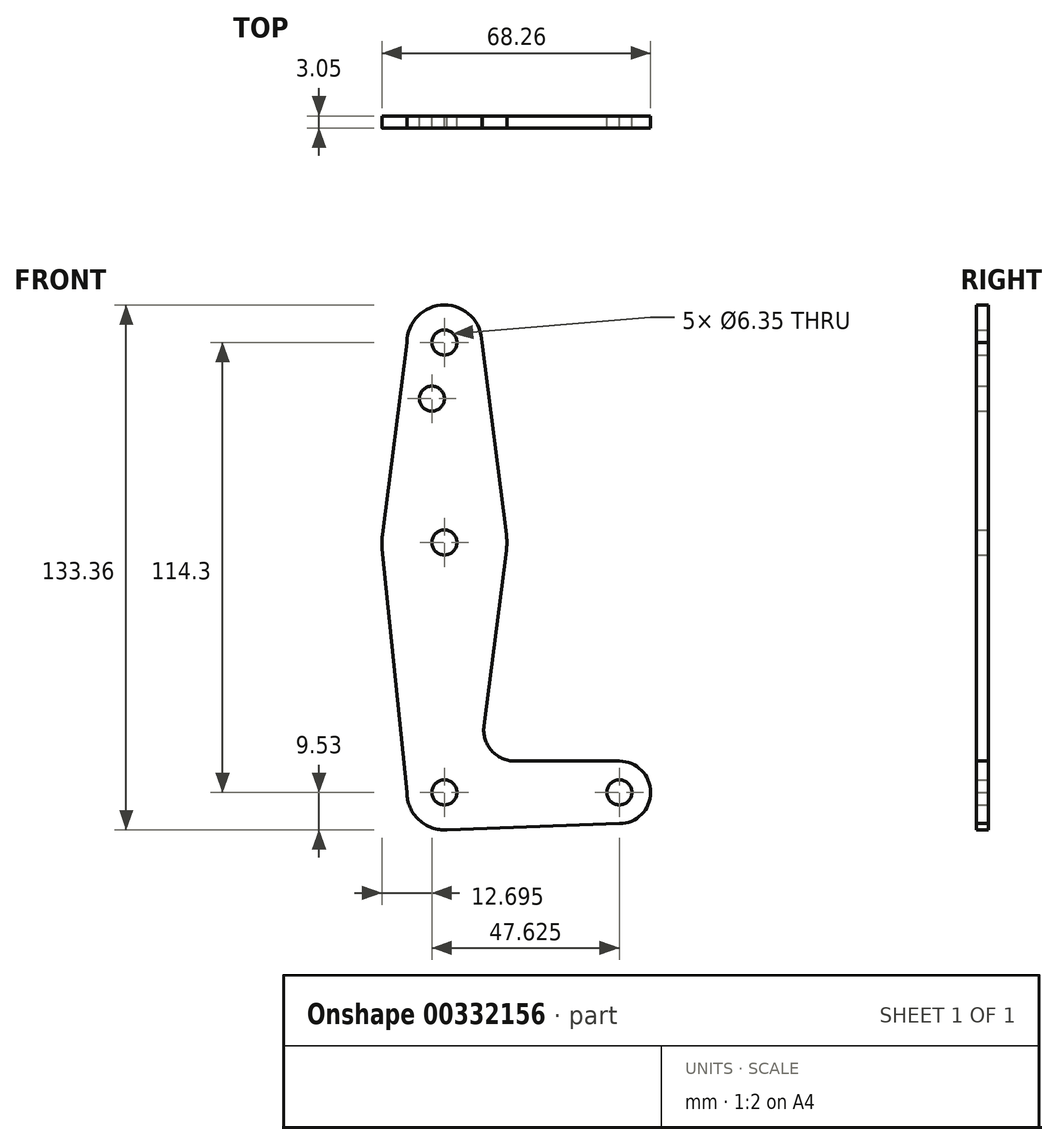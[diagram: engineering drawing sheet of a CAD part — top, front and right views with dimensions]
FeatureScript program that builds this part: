
annotation { "Feature Type Name" : "Feature", "Feature Type Description" : "" }
export const myFeature = defineFeature(function(context is Context, id is Id, definition is map)
    precondition{}
    {
        {
            var Q0;
            Q0=qCreatedBy(makeId("Front.planeOp"),FACE);
            var sketch = newSketch(context, id + "F0", { "sketchPlane" : qUnion([Q0])});
            skCircle(sketch, "E0", {"center": v(0, 0) * mm, "radius": 9.53 * mm});
            skLineSegment(sketch, "E1", {"start": v(0, 0) * mm, "end": v(0, 114.3) * mm, "construction": true});
            skLineSegment(sketch, "E2", {"start": v(0, 0) * mm, "end": v(44.45, 0) * mm, "construction": true});
            skCircle(sketch, "E3", {"center": v(0, 114.3) * mm, "radius": 9.53 * mm});
            skCircle(sketch, "E4", {"center": v(0, 63.5) * mm, "radius": 15.88 * mm});
            skCircle(sketch, "E5", {"center": v(44.45, 0) * mm, "radius": 7.94 * mm});
            skLineSegment(sketch, "E6", {"start": v(-9.53, 114.3) * mm, "end": v(-15.75, 65.5) * mm});
            skLineSegment(sketch, "E7", {"start": v(9.53, 114.3) * mm, "end": v(15.75, 65.5) * mm});
            skLineSegment(sketch, "E8", {"start": v(17.95, 7.94) * mm, "end": v(44.45, 7.94) * mm});
            skLineSegment(sketch, "E9", {"start": v(0, -9.52) * mm, "end": v(44.45, -7.94) * mm});
            skLineSegment(sketch, "E10", {"start": v(10.06, 16.9) * mm, "end": v(15.75, 61.5) * mm});
            skLineSegment(sketch, "E11", {"start": v(-9.53, 0) * mm, "end": v(-15.8, 61.9) * mm});
            skCircle(sketch, "E12", {"center": v(0, 114.3) * mm, "radius": 3.18 * mm});
            skCircle(sketch, "E13", {"center": v(0, 63.5) * mm, "radius": 3.18 * mm});
            skCircle(sketch, "E14", {"center": v(0, 0) * mm, "radius": 3.18 * mm});
            skCircle(sketch, "E15", {"center": v(44.45, 0) * mm, "radius": 3.18 * mm});
            skCircle(sketch, "E16", {"center": v(-3.18, 100.03) * mm, "radius": 3.18 * mm});
            skArc(sketch, "E17.filletArc", {"start": v(10.06, 16.9) * mm, "mid": v(11.98, 10.63) * mm, "end": v(17.95, 7.94) * mm});
            skSolve(sketch);
        }
        {
            var Q0;
            Q0 = qSketchRegion(id + "F0", true);
            extrude(context, id + "F1", {"entities" : qUnion([Q0]), "depth" : 3.05 * mm});
        }
    });
